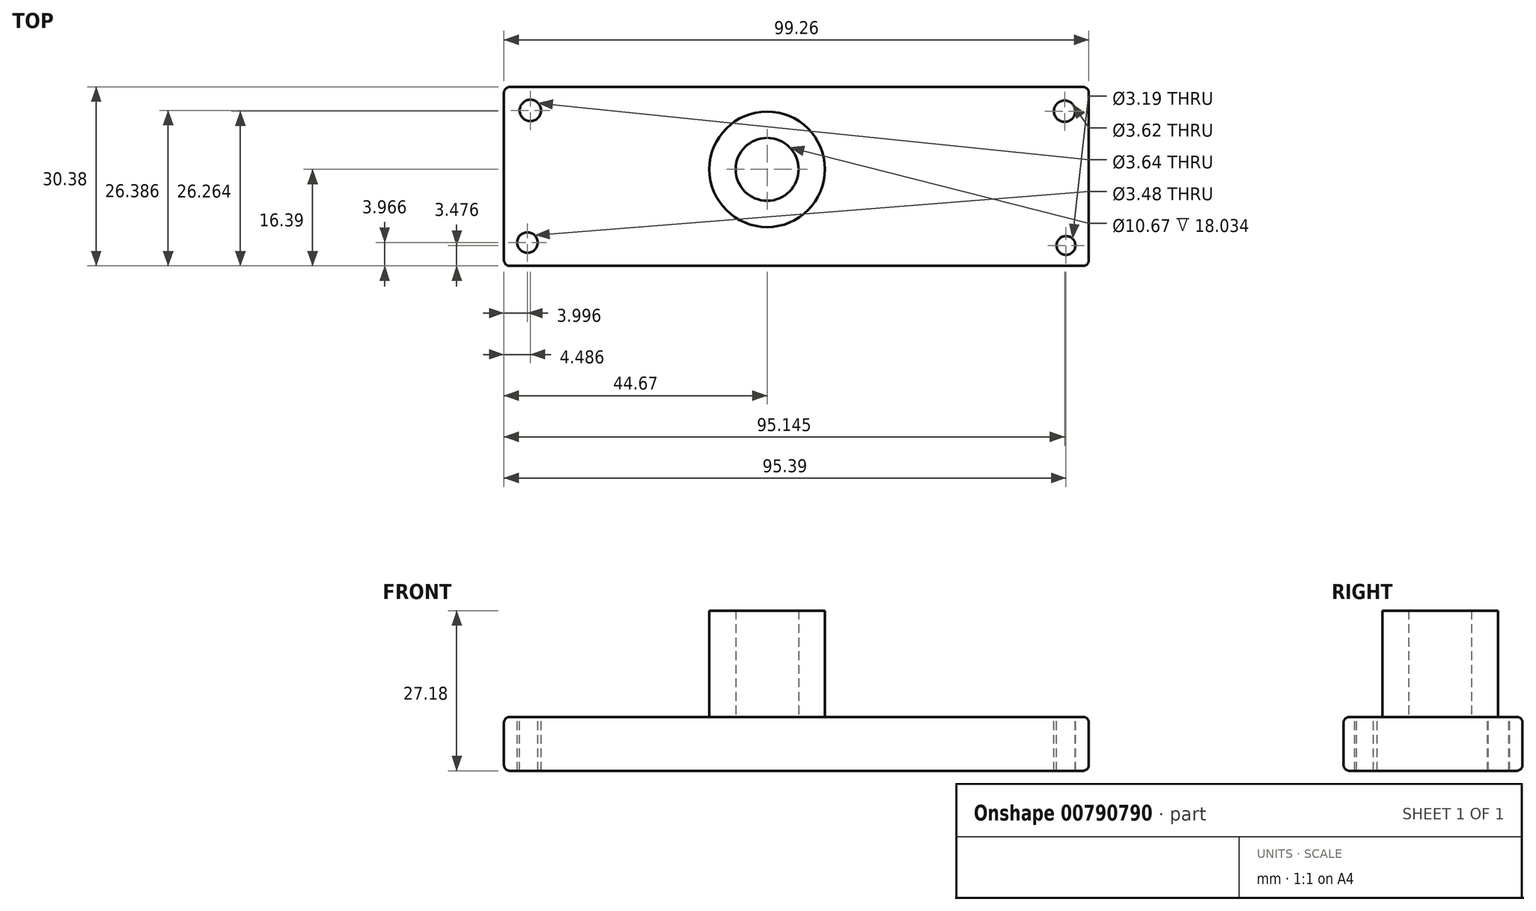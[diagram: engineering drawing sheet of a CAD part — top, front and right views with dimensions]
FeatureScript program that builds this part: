
annotation { "Feature Type Name" : "Feature", "Feature Type Description" : "" }
export const myFeature = defineFeature(function(context is Context, id is Id, definition is map)
    precondition{}
    {
        {
            var Q0;
            Q0=qCreatedBy(makeId("Top.planeOp"),FACE);
            var sketch = newSketch(context, id + "F0", { "sketchPlane" : qUnion([Q0])});
            skLineSegment(sketch, "E0.bottom", {"start": v(-44.67, 13.99) * mm, "end": v(54.6, 13.99) * mm});
            skLineSegment(sketch, "E0.top", {"start": v(-44.67, -16.4) * mm, "end": v(54.6, -16.4) * mm});
            skLineSegment(sketch, "E0.left", {"start": v(-44.67, 13.99) * mm, "end": v(-44.67, -16.4) * mm});
            skLineSegment(sketch, "E0.right", {"start": v(54.6, 13.99) * mm, "end": v(54.6, -16.4) * mm});
            skSolve(sketch);
        }
        {
            var Q0;
            Q0 = qSketchRegion(id + "F0", true);
            var Q1;
            Q1=makeQuery(id+"F0.imprint","IMPRINT",FACE,{"disambiguationData":[TD([[makeQuery(id+"F0.imprint","IMPRINT",EDGE,{"derivedFrom":sQuery(id+"F0.wireOp",EDGE,"E0.bottom")}),-1.0]])]});
            extrude(context, id + "F1", {"entities" : qUnion([Q0, Q1]), "depth" : 9.14 * mm, "offsetDistance" : 25.4 * mm});
        }
        {
            var Q0;
            Q0=makeQuery(id+"F1.opExtrude","CAP_EDGE",EDGE,{"disambiguationData":[OSD([sQuery(id+"F0.wireOp",EDGE,"E0.left")])],"isStart":false});
            var Q1;
            Q1=makeQuery(id+"F1.opExtrude","CAP_EDGE",EDGE,{"disambiguationData":[OSD([sQuery(id+"F0.wireOp",EDGE,"E0.bottom")])],"isStart":false});
            var Q2;
            Q2=makeQuery(id+"F1.opExtrude","CAP_EDGE",EDGE,{"disambiguationData":[OSD([sQuery(id+"F0.wireOp",EDGE,"E0.top")])],"isStart":false});
            var Q3;
            Q3=makeQuery(id+"F1.opExtrude","CAP_EDGE",EDGE,{"disambiguationData":[OSD([sQuery(id+"F0.wireOp",EDGE,"E0.right")])],"isStart":false});
            var Q4;
            Q4=makeQuery(id+"F1.opExtrude","CAP_EDGE",EDGE,{"disambiguationData":[OSD([sQuery(id+"F0.wireOp",EDGE,"E0.right")])],"isStart":true});
            var Q5;
            Q5=makeQuery(id+"F1.opExtrude","SWEPT_EDGE",EDGE,{"disambiguationData":[OSD([sQuery(id+"F0.wireOp",EDGE,"E0.bottom"),sQuery(id+"F0.wireOp",EDGE,"E0.right")])]});
            var Q6;
            Q6=makeQuery(id+"F1.opExtrude","SWEPT_EDGE",EDGE,{"disambiguationData":[OSD([sQuery(id+"F0.wireOp",EDGE,"E0.top"),sQuery(id+"F0.wireOp",EDGE,"E0.right")])]});
            var Q7;
            Q7=makeQuery(id+"F1.opExtrude","CAP_EDGE",EDGE,{"disambiguationData":[OSD([sQuery(id+"F0.wireOp",EDGE,"E0.bottom")])],"isStart":true});
            var Q8;
            Q8=makeQuery(id+"F1.opExtrude","SWEPT_EDGE",EDGE,{"disambiguationData":[OSD([sQuery(id+"F0.wireOp",EDGE,"E0.bottom"),sQuery(id+"F0.wireOp",EDGE,"E0.left")])]});
            var Q9;
            Q9=makeQuery(id+"F1.opExtrude","CAP_EDGE",EDGE,{"disambiguationData":[OSD([sQuery(id+"F0.wireOp",EDGE,"E0.left")])],"isStart":true});
            var Q10;
            Q10=makeQuery(id+"F1.opExtrude","SWEPT_EDGE",EDGE,{"disambiguationData":[OSD([sQuery(id+"F0.wireOp",EDGE,"E0.top"),sQuery(id+"F0.wireOp",EDGE,"E0.left")])]});
            var Q11;
            Q11=makeQuery(id+"F1.opExtrude","CAP_EDGE",EDGE,{"disambiguationData":[OSD([sQuery(id+"F0.wireOp",EDGE,"E0.top")])],"isStart":true});
            fillet(context, id + "F2", {"entities" : qUnion([Q0, Q1, Q2, Q3, Q4, Q5, Q6, Q7, Q8, Q9, Q10, Q11]), "radius" : 1.02 * mm, "tangentPropagation" : true, "allowEdgeOverflow" : false});
        }
        {
            var Q0;
            Q0=makeQuery(id+"F1.opExtrude","CAP_FACE",FACE,{"disambiguationData":[OSD([sQuery(id+"F0.wireOp",EDGE,"E0.bottom"),sQuery(id+"F0.wireOp",EDGE,"E0.top"),sQuery(id+"F0.wireOp",EDGE,"E0.left"),sQuery(id+"F0.wireOp",EDGE,"E0.right")])],"isStart":false});
            var sketch = newSketch(context, id + "F3", { "sketchPlane" : qUnion([Q0])});
            skCircle(sketch, "E1", {"center": v(-40.18, 10) * mm, "radius": 1.82 * mm});
            skCircle(sketch, "E2", {"center": v(-40.67, -12.42) * mm, "radius": 1.74 * mm});
            skCircle(sketch, "E3", {"center": v(50.47, 9.87) * mm, "radius": 1.8 * mm});
            skCircle(sketch, "E4", {"center": v(50.72, -12.91) * mm, "radius": 1.6 * mm});
            skCircle(sketch, "E5", {"center": v(0, 0) * mm, "radius": 9.8 * mm});
            skCircle(sketch, "E6", {"center": v(0, 0) * mm, "radius": 5.34 * mm});
            skSolve(sketch);
        }
        {
            var Q0;
            Q0=makeQuery(id+"F3.imprint","IMPRINT",FACE,{"disambiguationData":[TD([[makeQuery(id+"F3.imprint","IMPRINT",EDGE,{"derivedFrom":sQuery(id+"F3.wireOp",EDGE,"E4")}),1.0]])]});
            var Q1;
            Q1=makeQuery(id+"F3.imprint","IMPRINT",FACE,{"disambiguationData":[TD([[makeQuery(id+"F3.imprint","IMPRINT",EDGE,{"derivedFrom":sQuery(id+"F3.wireOp",EDGE,"E3")}),1.0]])]});
            var Q2;
            Q2=makeQuery(id+"F3.imprint","IMPRINT",FACE,{"disambiguationData":[TD([[makeQuery(id+"F3.imprint","IMPRINT",EDGE,{"derivedFrom":sQuery(id+"F3.wireOp",EDGE,"E1")}),1.0]])]});
            var Q3;
            Q3=makeQuery(id+"F3.imprint","IMPRINT",FACE,{"disambiguationData":[TD([[makeQuery(id+"F3.imprint","IMPRINT",EDGE,{"derivedFrom":sQuery(id+"F3.wireOp",EDGE,"E2")}),1.0]])]});
            extrude(context, id + "F4", {"entities" : qUnion([Q0, Q1, Q2, Q3]), "operationType" : NewBodyOperationType.REMOVE, "endBound" : BoundingType.THROUGH_ALL, "oppositeDirection" : true, "depth" : 25.4 * mm, "offsetDistance" : 25.4 * mm});
        }
        {
            var Q0;
            Q0=makeQuery(id+"F3.imprint","IMPRINT",FACE,{"disambiguationData":[TD([[makeQuery(id+"F3.imprint","IMPRINT",EDGE,{"derivedFrom":sQuery(id+"F3.wireOp",EDGE,"E5")}),1.0]])]});
            extrude(context, id + "F5", {"entities" : qUnion([Q0]), "operationType" : NewBodyOperationType.ADD, "depth" : 18.03 * mm, "offsetDistance" : 25.4 * mm});
        }
    });
